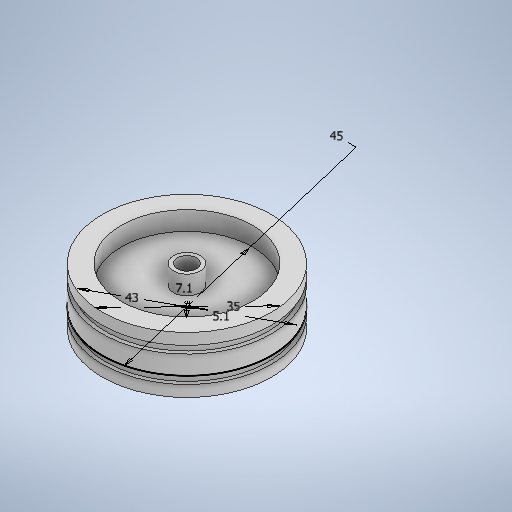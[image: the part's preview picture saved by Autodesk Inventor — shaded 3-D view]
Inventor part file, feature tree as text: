
AUTODESK INVENTOR PART (.ipt)
format: ipt  version: 2025.1 (Build 291241020, 241B)  size: 313,856 bytes
history: native  units: mm
features: extrude x7, sketch x2
ambient origin geometry x8: Origin, YZ Plane, XZ Plane, XY Plane, X Axis, Y Axis, Z Axis, Center Point
bodies: Solid1 (feature_tree)
feature tree (9):
  sketch  "Sketch1"  dims[d0=45.0mm d1=5.1mm]
  extrude  "Extrusion1"  Depth=5.1mm
  extrude  "Extrusion2"  Depth=5.0mm TaperAngle=0.0deg
  extrude  "Extrusion3"  Depth=10.0mm TaperAngle=0.0deg
  extrude  "Extrusion4"  Depth=5.0mm TaperAngle=0.0deg
  extrude  "Extrusion5"  Depth=10.0mm
  extrude  "Extrusion6"  Depth=2.0mm TaperAngle=0.0deg
  extrude  "Extrusion7"  Depth=10.0mm
  sketch  "Sketch2"  dims[d2=35.0mm d3=5.0mm d4=0.0mm d5=10.0mm d6=0.0mm d7=5.0mm d8=0.0mm d9=43.0mm d10=2.0mm d11=0.0mm d12=45.0mm d13=43.0mm d14=2.0mm d15=0.0mm d16=7.1mm d17=5.0mm d18=0.0mm d19=10.0mm d20=0.0mm]
